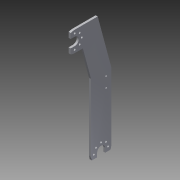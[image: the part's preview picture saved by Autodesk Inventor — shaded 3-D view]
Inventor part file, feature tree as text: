
AUTODESK INVENTOR PART (.ipt)
format: ipt  version: 2013 (Build 170138000, 138)  size: 197,120 bytes
history: native  units: mm
features: sketch x6, extrude x4, hole x2, pattern_circular x2, other x1
ambient origin geometry x8: Origin, YZ Plane, XZ Plane, XY Plane, X Axis, Y Axis, Z Axis, Center Point
feature tree (15):
  other  "ソリッド1"
  extrude  "押し出し1"  Depth=40.0mm
  extrude  "押し出し2"  Depth=20.0mm
  extrude  "押し出し3"  Depth=120.0mm
  hole  "穴1"  [1 undecoded]
  pattern_circular  "円形状パターン1"  [2 undecoded]
  pattern_circular  "円形状パターン2"  Count=2  [1 undecoded]
  hole  "穴2"  [1 undecoded]
  extrude  "押し出し4"  Depth=70.0mm
  sketch  "スケッチ1"
  sketch  "スケッチ2"
  sketch  "スケッチ3"
  sketch  "スケッチ4"
  sketch  "スケッチ5"
  sketch  "スケッチ6"
note: 5 required parameter values undecoded (feature->parameter linkage not recoverable at this tier; creation-order binding heuristic only, values carry confidence <= 0.55)
